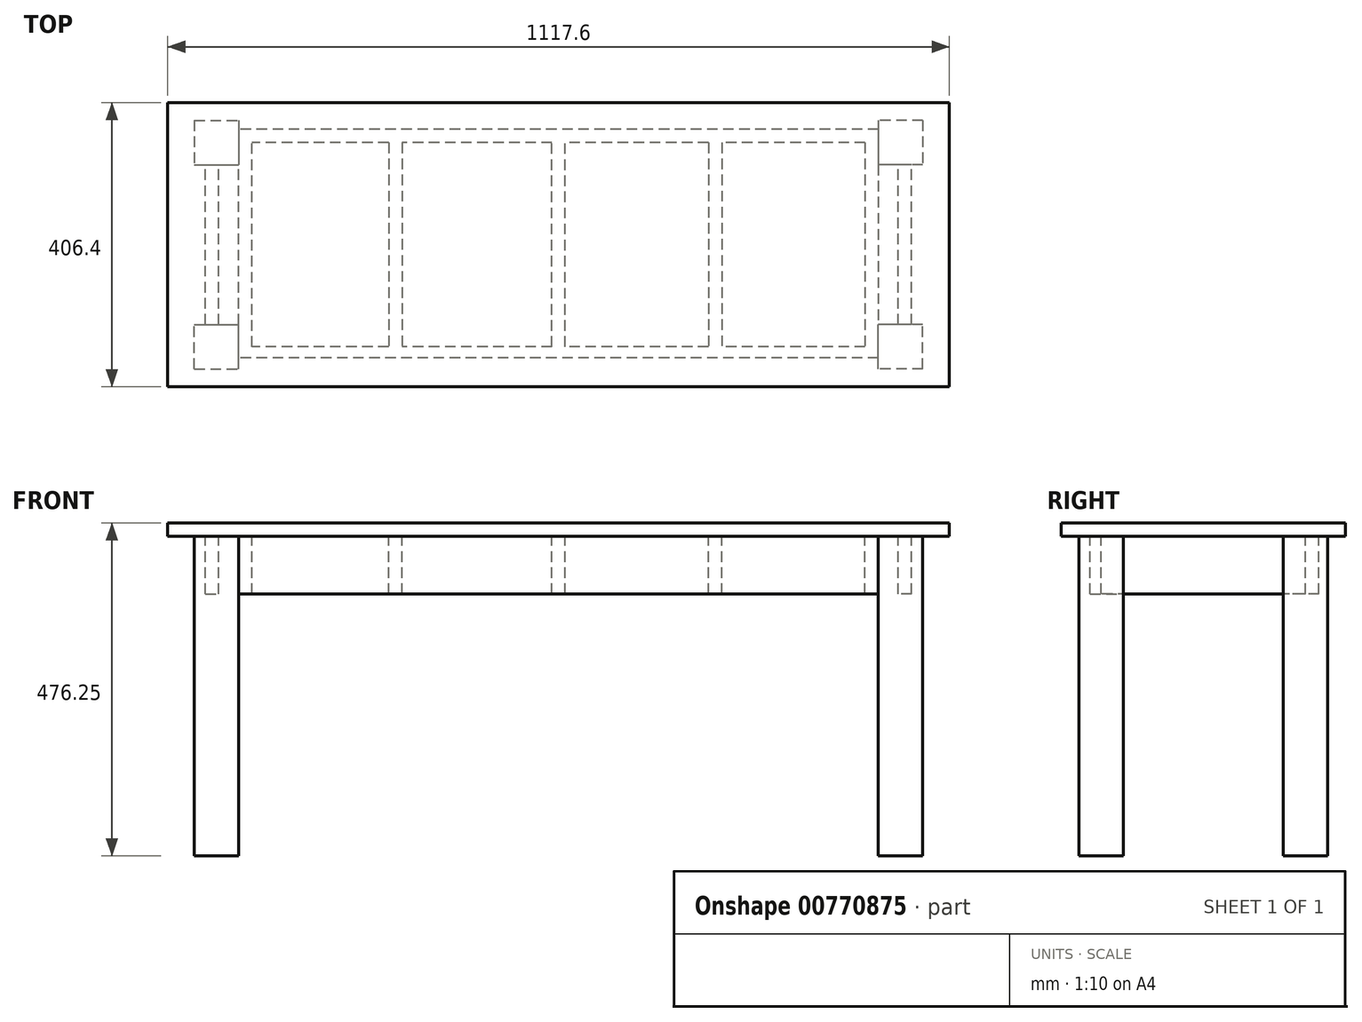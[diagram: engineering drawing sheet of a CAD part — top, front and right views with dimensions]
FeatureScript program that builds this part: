
annotation { "Feature Type Name" : "Feature", "Feature Type Description" : "" }
export const myFeature = defineFeature(function(context is Context, id is Id, definition is map)
    precondition{}
    {
        {
            var Q0;
            Q0=qCreatedBy(makeId("Top.planeOp"),FACE);
            var sketch = newSketch(context, id + "F0", { "sketchPlane" : qUnion([Q0])});
            skLineSegment(sketch, "E0.bottom", {"start": v(558.8, 203.2) * mm, "end": v(-558.8, 203.2) * mm});
            skLineSegment(sketch, "E0.top", {"start": v(558.8, -203.2) * mm, "end": v(-558.8, -203.2) * mm});
            skLineSegment(sketch, "E0.left", {"start": v(558.8, 203.2) * mm, "end": v(558.8, -203.2) * mm});
            skLineSegment(sketch, "E0.right", {"start": v(-558.8, 203.2) * mm, "end": v(-558.8, -203.2) * mm});
            skPoint(sketch, "E0.middle", {"position": v(0, 0) * mm});
            skSolve(sketch);
        }
        {
            var Q0;
            Q0=makeQuery(id+"F0.imprint","IMPRINT",FACE,{"disambiguationData":[TD([[makeQuery(id+"F0.imprint","IMPRINT",EDGE,{"derivedFrom":sQuery(id+"F0.wireOp",EDGE,"E0.bottom")}),1.0]])]});
            extrude(context, id + "F1", {"entities" : qUnion([Q0]), "depth" : 19.05 * mm, "offsetDistance" : 25.4 * mm});
        }
        {
            var Q0;
            Q0=makeQuery(id+"F1.opExtrude","CAP_FACE",FACE,{"disambiguationData":[OSD([sQuery(id+"F0.wireOp",EDGE,"E0.bottom"),sQuery(id+"F0.wireOp",EDGE,"E0.top"),sQuery(id+"F0.wireOp",EDGE,"E0.left"),sQuery(id+"F0.wireOp",EDGE,"E0.right")])],"isStart":true});
            var sketch = newSketch(context, id + "F2", { "sketchPlane" : qUnion([Q0])});
            skLineSegment(sketch, "E1", {"start": v(-558.8, 203.2) * mm, "end": v(-558.8, 177.8) * mm});
            skLineSegment(sketch, "E2", {"start": v(-558.8, 177.8) * mm, "end": v(-520.7, 177.8) * mm});
            skLineSegment(sketch, "E3.bottom", {"start": v(-520.7, 177.8) * mm, "end": v(-457.2, 177.8) * mm});
            skLineSegment(sketch, "E3.top", {"start": v(-520.7, 114.3) * mm, "end": v(-457.2, 114.3) * mm});
            skLineSegment(sketch, "E3.left", {"start": v(-520.7, 177.8) * mm, "end": v(-520.7, 114.3) * mm});
            skLineSegment(sketch, "E3.right", {"start": v(-457.2, 177.8) * mm, "end": v(-457.2, 114.3) * mm});
            skSolve(sketch);
        }
        {
            var Q0;
            Q0=makeQuery(id+"F2.imprint","IMPRINT",FACE,{"disambiguationData":[TD([[makeQuery(id+"F2.imprint","IMPRINT",EDGE,{"derivedFrom":sQuery(id+"F2.wireOp",EDGE,"E3.bottom")}),-1.0]])]});
            extrude(context, id + "F3", {"entities" : qUnion([Q0]), "operationType" : NewBodyOperationType.ADD, "depth" : 457.2 * mm, "offsetDistance" : 25.4 * mm});
        }
        {
            var Q0;
            Q0=makeQuery(id+"F1.opExtrude","SWEPT_BODY",BODY,{"disambiguationData":[OSD([sQuery(id+"F0.wireOp",EDGE,"E0.bottom"),sQuery(id+"F0.wireOp",EDGE,"E0.top"),sQuery(id+"F0.wireOp",EDGE,"E0.left"),sQuery(id+"F0.wireOp",EDGE,"E0.right")])]});
            var Q1;
            Q1=qCreatedBy(makeId("Front.planeOp"),FACE);
            mirror(context, id + "F4", {"operationType" : NewBodyOperationType.ADD, "entities" : qUnion([Q0]), "mirrorPlane" : qUnion([Q1])});
        }
        {
            var Q0;
            Q0=makeQuery(id+"F1.opExtrude","SWEPT_BODY",BODY,{"disambiguationData":[OSD([sQuery(id+"F0.wireOp",EDGE,"E0.bottom"),sQuery(id+"F0.wireOp",EDGE,"E0.top"),sQuery(id+"F0.wireOp",EDGE,"E0.left"),sQuery(id+"F0.wireOp",EDGE,"E0.right")])]});
            var Q1;
            Q1=qCreatedBy(makeId("Right.planeOp"),FACE);
            mirror(context, id + "F5", {"operationType" : NewBodyOperationType.ADD, "entities" : qUnion([Q0]), "mirrorPlane" : qUnion([Q1])});
        }
        {
            var Q0;
            Q0=makeQuery(id+"F1.opExtrude","CAP_FACE",FACE,{"disambiguationData":[OSD([sQuery(id+"F0.wireOp",EDGE,"E0.bottom"),sQuery(id+"F0.wireOp",EDGE,"E0.top"),sQuery(id+"F0.wireOp",EDGE,"E0.left"),sQuery(id+"F0.wireOp",EDGE,"E0.right")])],"isStart":true});
            var sketch = newSketch(context, id + "F6", { "sketchPlane" : qUnion([Q0])});
            skLineSegment(sketch, "E4", {"start": v(520.7, 114.3) * mm, "end": v(504.83, 114.3) * mm});
            skLineSegment(sketch, "E5.bottom", {"start": v(504.83, 114.3) * mm, "end": v(485.78, 114.3) * mm});
            skLineSegment(sketch, "E5.top", {"start": v(504.83, -114.3) * mm, "end": v(485.78, -114.3) * mm});
            skLineSegment(sketch, "E5.left", {"start": v(504.83, 114.3) * mm, "end": v(504.83, -114.3) * mm});
            skLineSegment(sketch, "E5.right", {"start": v(485.78, 114.3) * mm, "end": v(485.78, -114.3) * mm});
            skSolve(sketch);
        }
        {
            var Q0;
            Q0=qSketchRegion(id+"F6",true);
            extrude(context, id + "F7", {"entities" : qUnion([Q0]), "operationType" : NewBodyOperationType.ADD, "depth" : 82.55 * mm, "offsetDistance" : 25.4 * mm});
        }
        {
            var Q0;
            Q0=makeQuery(id+"F1.opExtrude","SWEPT_BODY",BODY,{"disambiguationData":[OSD([sQuery(id+"F0.wireOp",EDGE,"E0.bottom"),sQuery(id+"F0.wireOp",EDGE,"E0.top"),sQuery(id+"F0.wireOp",EDGE,"E0.left"),sQuery(id+"F0.wireOp",EDGE,"E0.right")])]});
            var Q1;
            Q1=qCreatedBy(makeId("Right.planeOp"),FACE);
            mirror(context, id + "F8", {"operationType" : NewBodyOperationType.ADD, "entities" : qUnion([Q0]), "mirrorPlane" : qUnion([Q1])});
        }
        {
            var Q0;
            Q0=makeQuery(id+"F1.opExtrude","CAP_FACE",FACE,{"disambiguationData":[OSD([sQuery(id+"F0.wireOp",EDGE,"E0.bottom"),sQuery(id+"F0.wireOp",EDGE,"E0.top"),sQuery(id+"F0.wireOp",EDGE,"E0.left"),sQuery(id+"F0.wireOp",EDGE,"E0.right")])],"isStart":true});
            var sketch = newSketch(context, id + "F9", { "sketchPlane" : qUnion([Q0])});
            skLineSegment(sketch, "E6", {"start": v(457.2, -177.8) * mm, "end": v(457.2, -165.1) * mm});
            skLineSegment(sketch, "E7", {"start": v(457.2, -165.1) * mm, "end": v(457.2, -177.8) * mm});
            skLineSegment(sketch, "E8.bottom", {"start": v(457.2, -165.1) * mm, "end": v(-457.2, -165.1) * mm});
            skLineSegment(sketch, "E8.top", {"start": v(457.2, -146.05) * mm, "end": v(-457.2, -146.05) * mm});
            skLineSegment(sketch, "E8.left", {"start": v(457.2, -165.1) * mm, "end": v(457.2, -146.05) * mm});
            skLineSegment(sketch, "E8.right", {"start": v(-457.2, -165.1) * mm, "end": v(-457.2, -146.05) * mm});
            skSolve(sketch);
        }
        {
            var Q0;
            Q0=qSketchRegion(id+"F9",true);
            extrude(context, id + "F10", {"entities" : qUnion([Q0]), "operationType" : NewBodyOperationType.ADD, "depth" : 82.55 * mm, "offsetDistance" : 25.4 * mm});
        }
        {
            var Q0;
            Q0=makeQuery(id+"F1.opExtrude","CAP_FACE",FACE,{"disambiguationData":[OSD([sQuery(id+"F0.wireOp",EDGE,"E0.bottom"),sQuery(id+"F0.wireOp",EDGE,"E0.top"),sQuery(id+"F0.wireOp",EDGE,"E0.left"),sQuery(id+"F0.wireOp",EDGE,"E0.right")])],"isStart":true});
            var sketch = newSketch(context, id + "F11", { "sketchPlane" : qUnion([Q0])});
            skLineSegment(sketch, "E9", {"start": v(457.2, 177.8) * mm, "end": v(457.2, 161.93) * mm});
            skLineSegment(sketch, "E10.bottom", {"start": v(457.2, 161.93) * mm, "end": v(-457.2, 161.93) * mm});
            skLineSegment(sketch, "E10.top", {"start": v(457.2, 146.05) * mm, "end": v(-457.2, 146.05) * mm});
            skLineSegment(sketch, "E10.left", {"start": v(457.2, 161.93) * mm, "end": v(457.2, 146.05) * mm});
            skLineSegment(sketch, "E10.right", {"start": v(-457.2, 161.93) * mm, "end": v(-457.2, 146.05) * mm});
            skSolve(sketch);
        }
        {
            var Q0;
            Q0=qSketchRegion(id+"F11",true);
            extrude(context, id + "F12", {"entities" : qUnion([Q0]), "operationType" : NewBodyOperationType.ADD, "depth" : 82.55 * mm, "offsetDistance" : 25.4 * mm});
        }
        {
            var Q0;
            Q0=makeQuery(id+"F5.opPattern","COPY",FACE,{"derivedFrom":makeQuery(id+"F4.opPattern","COPY",FACE,{"derivedFrom":makeQuery(id+"F3.opExtrude","SWEPT_FACE",FACE,{"disambiguationData":[OSD([sQuery(id+"F2.wireOp",EDGE,"E3.right")])]}),"instanceName":"1"}),"instanceName":"1"});
            var sketch = newSketch(context, id + "F13", { "sketchPlane" : qUnion([Q0])});
            skLineSegment(sketch, "E11.bottom", {"start": v(-146.05, -82.55) * mm, "end": v(146.12, -82.55) * mm});
            skLineSegment(sketch, "E11.top", {"start": v(-146.05, 0) * mm, "end": v(146.12, 0) * mm});
            skLineSegment(sketch, "E11.left", {"start": v(-146.05, -82.55) * mm, "end": v(-146.05, 0) * mm});
            skLineSegment(sketch, "E11.right", {"start": v(146.12, -82.55) * mm, "end": v(146.12, 0) * mm});
            skSolve(sketch);
        }
        {
            var Q0;
            Q0=qSketchRegion(id+"F13",true);
            extrude(context, id + "F14", {"entities" : qUnion([Q0]), "operationType" : NewBodyOperationType.ADD, "depth" : 19.05 * mm, "offsetDistance" : 25.4 * mm});
        }
        {
            var Q0;
            Q0=makeQuery(id+"F3.opExtrude","SWEPT_FACE",FACE,{"disambiguationData":[OSD([sQuery(id+"F2.wireOp",EDGE,"E3.right")])]});
            var sketch = newSketch(context, id + "F15", { "sketchPlane" : qUnion([Q0])});
            skLineSegment(sketch, "E12.bottom", {"start": v(-146.05, -82.55) * mm, "end": v(146.26, -82.55) * mm});
            skLineSegment(sketch, "E12.top", {"start": v(-146.05, 0) * mm, "end": v(146.26, 0) * mm});
            skLineSegment(sketch, "E12.left", {"start": v(-146.05, -82.55) * mm, "end": v(-146.05, 0) * mm});
            skLineSegment(sketch, "E12.right", {"start": v(146.26, -82.55) * mm, "end": v(146.26, 0) * mm});
            skSolve(sketch);
        }
        {
            var Q0;
            Q0=qSketchRegion(id+"F15",true);
            extrude(context, id + "F16", {"entities" : qUnion([Q0]), "operationType" : NewBodyOperationType.ADD, "depth" : 19.05 * mm, "offsetDistance" : 25.4 * mm});
        }
        {
            var Q0;
            {var subQ0=makeQuery(id+"F10.opExtrude","SWEPT_FACE",FACE,{"disambiguationData":[OSD([sQuery(id+"F9.wireOp",EDGE,"E8.top")])]});var subQ5=makeQuery(id+"F3.opExtrude","SWEPT_FACE",FACE,{"disambiguationData":[OSD([sQuery(id+"F2.wireOp",EDGE,"E3.top")])]});var subQ7=makeQuery(id+"F7.opExtrude","SWEPT_FACE",FACE,{"disambiguationData":[OSD([sQuery(id+"F6.wireOp",EDGE,"E5.right")])]});Q0=makeQuery(id+"F16.boolean.opBoolean","SPLIT",FACE,{"disambiguationData":[TD([subQ0])],"derivedFrom":makeQuery(id+"F14.boolean.opBoolean","SPLIT",FACE,{"disambiguationData":[TD([subQ5])],"derivedFrom":makeQuery(id+"F12.boolean.opBoolean","SPLIT",FACE,{"disambiguationData":[TD([subQ7])],"derivedFrom":makeQuery(id+"F1.opExtrude","CAP_FACE",FACE,{"disambiguationData":[OSD([sQuery(id+"F0.wireOp",EDGE,"E0.bottom"),sQuery(id+"F0.wireOp",EDGE,"E0.top"),sQuery(id+"F0.wireOp",EDGE,"E0.left"),sQuery(id+"F0.wireOp",EDGE,"E0.right")])],"isStart":true})})})});}
            var sketch = newSketch(context, id + "F17", { "sketchPlane" : qUnion([Q0])});
            skLineSegment(sketch, "E13.bottom", {"start": v(9.53, 146.05) * mm, "end": v(-9.53, 146.05) * mm});
            skLineSegment(sketch, "E13.top", {"start": v(9.53, -146.05) * mm, "end": v(-9.53, -146.05) * mm});
            skLineSegment(sketch, "E13.left", {"start": v(9.53, 146.05) * mm, "end": v(9.53, -146.05) * mm});
            skLineSegment(sketch, "E13.right", {"start": v(-9.53, 146.05) * mm, "end": v(-9.53, -146.05) * mm});
            skPoint(sketch, "E13.middle", {"position": v(0, 0) * mm});
            skSolve(sketch);
        }
        {
            var Q0;
            Q0=qSketchRegion(id+"F17",true);
            extrude(context, id + "F18", {"entities" : qUnion([Q0]), "operationType" : NewBodyOperationType.ADD, "depth" : 82.55 * mm, "offsetDistance" : 25.4 * mm});
        }
        {
            var Q0;
            {var subQ0=makeQuery(id+"F10.opExtrude","SWEPT_FACE",FACE,{"disambiguationData":[OSD([sQuery(id+"F9.wireOp",EDGE,"E8.top")])]});var subQ6=makeQuery(id+"F3.opExtrude","SWEPT_FACE",FACE,{"disambiguationData":[OSD([sQuery(id+"F2.wireOp",EDGE,"E3.top")])]});var subQ8=makeQuery(id+"F7.opExtrude","SWEPT_FACE",FACE,{"disambiguationData":[OSD([sQuery(id+"F6.wireOp",EDGE,"E5.right")])]});Q0=makeQuery(id+"F18.boolean.opBoolean","SPLIT",FACE,{"disambiguationData":[TD([makeQuery(id+"F18.opExtrude","SWEPT_FACE",FACE,{"disambiguationData":[OSD([sQuery(id+"F17.wireOp",EDGE,"E13.right")])]})])],"derivedFrom":makeQuery(id+"F16.boolean.opBoolean","SPLIT",FACE,{"disambiguationData":[TD([subQ0])],"derivedFrom":makeQuery(id+"F14.boolean.opBoolean","SPLIT",FACE,{"disambiguationData":[TD([subQ6])],"derivedFrom":makeQuery(id+"F12.boolean.opBoolean","SPLIT",FACE,{"disambiguationData":[TD([subQ8])],"derivedFrom":makeQuery(id+"F1.opExtrude","CAP_FACE",FACE,{"disambiguationData":[OSD([sQuery(id+"F0.wireOp",EDGE,"E0.bottom"),sQuery(id+"F0.wireOp",EDGE,"E0.top"),sQuery(id+"F0.wireOp",EDGE,"E0.left"),sQuery(id+"F0.wireOp",EDGE,"E0.right")])],"isStart":true})})})})});}
            var sketch = newSketch(context, id + "F19", { "sketchPlane" : qUnion([Q0])});
            skLineSegment(sketch, "E14.bottom", {"start": v(-223.84, -146.05) * mm, "end": v(-242.89, -146.05) * mm});
            skLineSegment(sketch, "E14.top", {"start": v(-223.84, 438.15) * mm, "end": v(-242.89, 438.15) * mm});
            skLineSegment(sketch, "E14.left", {"start": v(-223.84, -146.05) * mm, "end": v(-223.84, 438.15) * mm});
            skLineSegment(sketch, "E14.right", {"start": v(-242.89, -146.05) * mm, "end": v(-242.89, 438.15) * mm});
            skPoint(sketch, "E14.middle", {"position": v(-233.36, 146.05) * mm});
            skLineSegment(sketch, "E15.bottom", {"start": v(-242.89, 146.05) * mm, "end": v(-223.84, 146.05) * mm});
            skLineSegment(sketch, "E15.top", {"start": v(-242.89, -146.05) * mm, "end": v(-223.84, -146.05) * mm});
            skLineSegment(sketch, "E15.left", {"start": v(-242.89, 146.05) * mm, "end": v(-242.89, -146.05) * mm});
            skLineSegment(sketch, "E15.right", {"start": v(-223.84, 146.05) * mm, "end": v(-223.84, -146.05) * mm});
            skSolve(sketch);
        }
        {
            var Q0;
            Q0=makeQuery(id+"F19.imprint","IMPRINT",FACE,{"disambiguationData":[TD([[makeQuery(id+"F19.imprint","IMPRINT",EDGE,{"derivedFrom":sQuery(id+"F19.wireOp",EDGE,"E15.bottom")}),1.0]])]});
            extrude(context, id + "F20", {"entities" : qUnion([Q0]), "operationType" : NewBodyOperationType.ADD, "depth" : 82.55 * mm, "offsetDistance" : 25.4 * mm});
        }
        {
            var Q0;
            {var subQ0=makeQuery(id+"F10.opExtrude","SWEPT_FACE",FACE,{"disambiguationData":[OSD([sQuery(id+"F9.wireOp",EDGE,"E8.top")])]});var subQ5=makeQuery(id+"F3.opExtrude","SWEPT_FACE",FACE,{"disambiguationData":[OSD([sQuery(id+"F2.wireOp",EDGE,"E3.top")])]});var subQ7=makeQuery(id+"F7.opExtrude","SWEPT_FACE",FACE,{"disambiguationData":[OSD([sQuery(id+"F6.wireOp",EDGE,"E5.right")])]});Q0=makeQuery(id+"F18.boolean.opBoolean","SPLIT",FACE,{"disambiguationData":[TD([makeQuery(id+"F18.opExtrude","SWEPT_FACE",FACE,{"disambiguationData":[OSD([sQuery(id+"F17.wireOp",EDGE,"E13.left")])]})])],"derivedFrom":makeQuery(id+"F16.boolean.opBoolean","SPLIT",FACE,{"disambiguationData":[TD([subQ0])],"derivedFrom":makeQuery(id+"F14.boolean.opBoolean","SPLIT",FACE,{"disambiguationData":[TD([subQ5])],"derivedFrom":makeQuery(id+"F12.boolean.opBoolean","SPLIT",FACE,{"disambiguationData":[TD([subQ7])],"derivedFrom":makeQuery(id+"F1.opExtrude","CAP_FACE",FACE,{"disambiguationData":[OSD([sQuery(id+"F0.wireOp",EDGE,"E0.bottom"),sQuery(id+"F0.wireOp",EDGE,"E0.top"),sQuery(id+"F0.wireOp",EDGE,"E0.left"),sQuery(id+"F0.wireOp",EDGE,"E0.right")])],"isStart":true})})})})});}
            var sketch = newSketch(context, id + "F21", { "sketchPlane" : qUnion([Q0])});
            skLineSegment(sketch, "E16.bottom", {"start": v(233.36, -146.05) * mm, "end": v(214.31, -146.05) * mm});
            skLineSegment(sketch, "E16.top", {"start": v(233.36, 438.15) * mm, "end": v(214.31, 438.15) * mm});
            skLineSegment(sketch, "E16.left", {"start": v(233.36, -146.05) * mm, "end": v(233.36, 438.15) * mm});
            skLineSegment(sketch, "E16.right", {"start": v(214.31, -146.05) * mm, "end": v(214.31, 438.15) * mm});
            skPoint(sketch, "E16.middle", {"position": v(223.84, 146.05) * mm});
            skLineSegment(sketch, "E17.bottom", {"start": v(214.31, 146.05) * mm, "end": v(233.36, 146.05) * mm});
            skLineSegment(sketch, "E17.top", {"start": v(214.31, -146.05) * mm, "end": v(233.36, -146.05) * mm});
            skLineSegment(sketch, "E17.left", {"start": v(214.31, 146.05) * mm, "end": v(214.31, -146.05) * mm});
            skLineSegment(sketch, "E17.right", {"start": v(233.36, 146.05) * mm, "end": v(233.36, -146.05) * mm});
            skSolve(sketch);
        }
        {
            var Q0;
            Q0=makeQuery(id+"F21.imprint","IMPRINT",FACE,{"disambiguationData":[TD([[makeQuery(id+"F21.imprint","IMPRINT",EDGE,{"derivedFrom":sQuery(id+"F21.wireOp",EDGE,"E17.bottom")}),1.0]])]});
            extrude(context, id + "F22", {"entities" : qUnion([Q0]), "operationType" : NewBodyOperationType.ADD, "depth" : 82.55 * mm, "offsetDistance" : 25.4 * mm});
        }
    });
